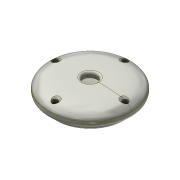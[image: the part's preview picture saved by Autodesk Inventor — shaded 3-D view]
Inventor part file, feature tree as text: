
AUTODESK INVENTOR PART (.ipt)
format: ipt  version: 2021 (Build 250183000, 183)  size: 784,384 bytes
history: native  units: mm
features: other x7, fillet x4, sketch x4, hole x2, projected_geometry x2, revolve x1, extrude x1
ambient origin geometry x8: Origin, YZ Plane, XZ Plane, XY Plane, X Axis, Y Axis, Z Axis, Center Point
bodies: Body1 (feature_tree), Body2 (feature_tree)
feature tree (21):
  other  "Твердое тело1"
  revolve  "Вращение1"
  fillet  "Сопряжение1"  Radius=3.0mm
  other  "РабПлоскость1"
  other  "Разделение1"
  fillet  "Сопряжение2"  Radius=2.0mm
  hole  "Отверстие1"  [1 undecoded]
  other  "РабПлоскость3"
  hole  "Отверстие2"  [1 undecoded]
  fillet  "Сопряжение3"  Radius=3.0mm
  other  "РабПлоскость4"
  extrude  "Выдавливание1"  Depth=2.0mm
  fillet  "Сопряжение4"  Radius=3.0mm
  sketch  "Эскиз1"
  sketch  "Эскиз3"
  projected_geometry  "Спроецированная петля1"
  projected_geometry  "Спроецированная петля2"
  sketch  "Эскиз5"
  sketch  "Эскиз6"
  other  "Твердое тело2"
  other  "Твердое тело3"
note: 2 required parameter values undecoded (feature->parameter linkage not recoverable at this tier; creation-order binding heuristic only, values carry confidence <= 0.55)
